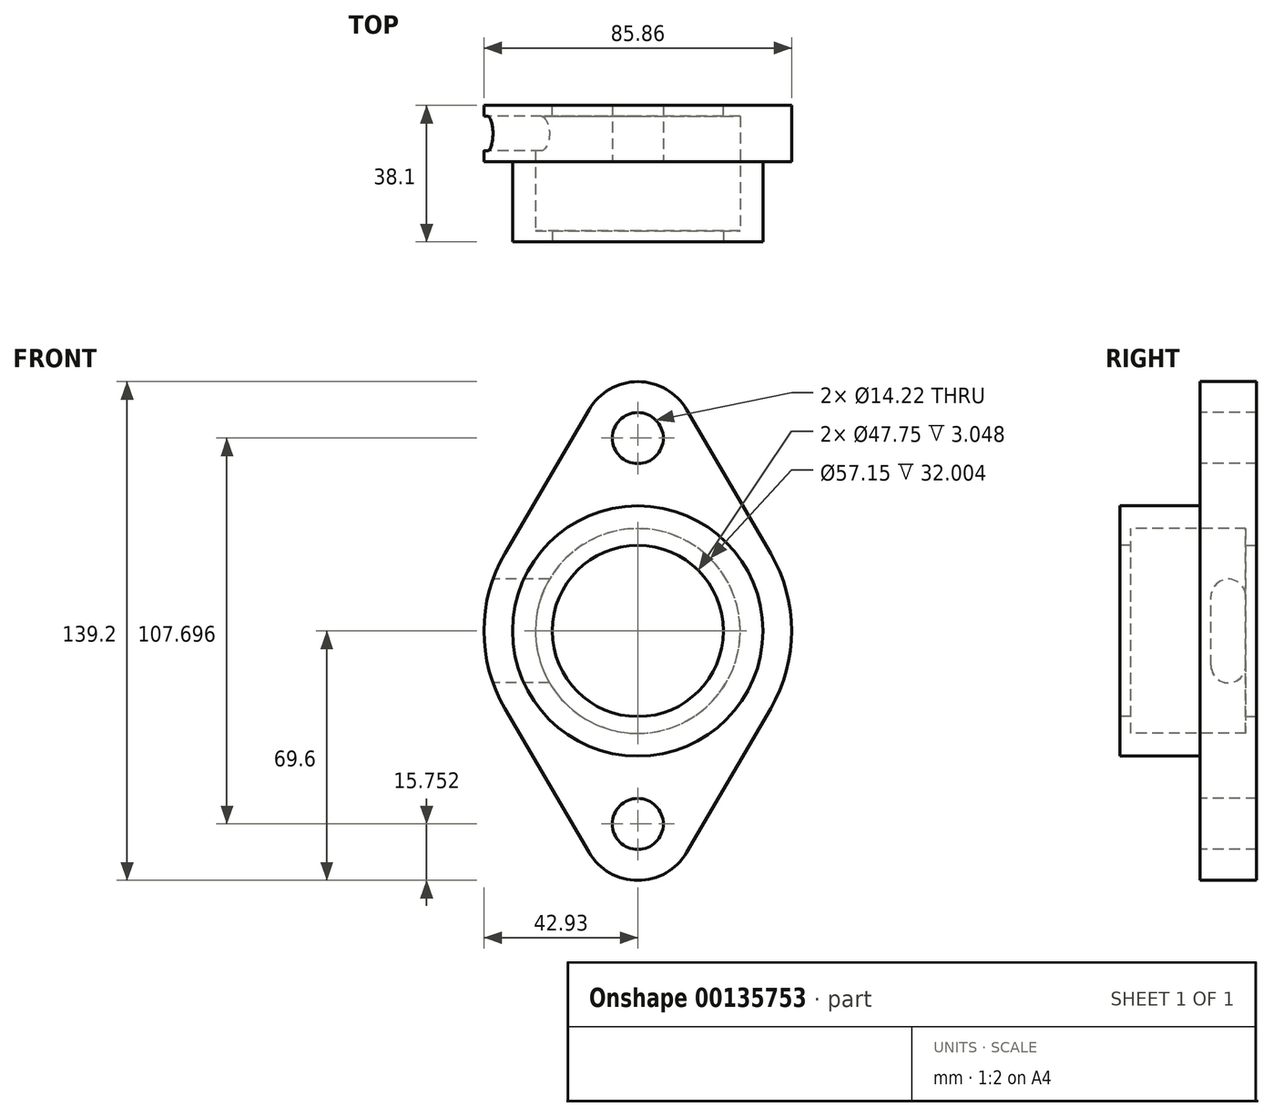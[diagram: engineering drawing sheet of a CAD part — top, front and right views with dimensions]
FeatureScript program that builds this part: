
annotation { "Feature Type Name" : "Feature", "Feature Type Description" : "" }
export const myFeature = defineFeature(function(context is Context, id is Id, definition is map)
    precondition{}
    {
        {
            var Q0;
            Q0=qCreatedBy(makeId("Front.planeOp"),FACE);
            var sketch = newSketch(context, id + "F0", { "sketchPlane" : qUnion([Q0])});
            skArc(sketch, "E0", {"start": v(-37.06, 21.67) * mm, "mid": v(-42.93, 0) * mm, "end": v(-37.06, -21.67) * mm});
            skLineSegment(sketch, "E1", {"start": v(-37.06, 21.67) * mm, "end": v(-13.6, 61.8) * mm});
            skLineSegment(sketch, "E2", {"start": v(37.06, 21.67) * mm, "end": v(13.6, 61.8) * mm});
            skLineSegment(sketch, "E3", {"start": v(-37.06, -21.67) * mm, "end": v(-13.6, -61.8) * mm});
            skLineSegment(sketch, "E4", {"start": v(37.06, -21.67) * mm, "end": v(13.6, -61.8) * mm});
            skArc(sketch, "E5", {"start": v(-13.6, -61.8) * mm, "mid": v(0, -69.6) * mm, "end": v(13.6, -61.8) * mm});
            skCircle(sketch, "E6", {"center": v(0, 53.85) * mm, "radius": 7.11 * mm});
            skArc(sketch, "E7", {"start": v(13.6, 61.8) * mm, "mid": v(0, 69.6) * mm, "end": v(-13.6, 61.8) * mm});
            skCircle(sketch, "E8", {"center": v(0, -53.85) * mm, "radius": 7.11 * mm});
            skArc(sketch, "E9.trimOffspring", {"start": v(37.06, -21.67) * mm, "mid": v(42.93, 0) * mm, "end": v(37.06, 21.67) * mm});
            skLineSegment(sketch, "E10", {"start": v(1.63, 0) * mm, "end": v(40.06, 0) * mm, "construction": true});
            skSolve(sketch);
        }
        {
            var Q0;
            Q0 = qSketchRegion(id + "F0", true);
            extrude(context, id + "F1", {"entities" : qUnion([Q0]), "oppositeDirection" : true, "depth" : 15.75 * mm});
        }
        {
            var Q0;
            Q0=makeQuery(id+"F1.opExtrude","CAP_FACE",FACE,{"disambiguationData":[OSD([sQuery(id+"F0.wireOp",EDGE,"E0"),sQuery(id+"F0.wireOp",EDGE,"E1"),sQuery(id+"F0.wireOp",EDGE,"E2"),sQuery(id+"F0.wireOp",EDGE,"E3"),sQuery(id+"F0.wireOp",EDGE,"E4"),sQuery(id+"F0.wireOp",EDGE,"E5"),sQuery(id+"F0.wireOp",EDGE,"E6"),sQuery(id+"F0.wireOp",EDGE,"E7"),sQuery(id+"F0.wireOp",EDGE,"E8"),sQuery(id+"F0.wireOp",EDGE,"E9.trimOffspring")])],"isStart":true});
            var sketch = newSketch(context, id + "F2", { "sketchPlane" : qUnion([Q0])});
            skCircle(sketch, "E11", {"center": v(0, 0) * mm, "radius": 34.93 * mm});
            skSolve(sketch);
        }
        {
            var Q0;
            Q0 = qSketchRegion(id + "F2", true);
            extrude(context, id + "F3", {"entities" : qUnion([Q0]), "operationType" : NewBodyOperationType.ADD, "depth" : 22.35 * mm});
        }
        {
            var Q0;
            Q0=makeQuery(id+"F3.opExtrude","CAP_FACE",FACE,{"disambiguationData":[OSD([sQuery(id+"F2.wireOp",EDGE,"E11")])],"isStart":false});
            var sketch = newSketch(context, id + "F4", { "sketchPlane" : qUnion([Q0])});
            skCircle(sketch, "E12", {"center": v(0, 0) * mm, "radius": 28.58 * mm});
            skSolve(sketch);
        }
        {
            var Q0;
            Q0 = qSketchRegion(id + "F4", true);
            extrude(context, id + "F5", {"entities" : qUnion([Q0]), "operationType" : NewBodyOperationType.REMOVE, "endBound" : BoundingType.THROUGH_ALL, "oppositeDirection" : true, "depth" : 25.4 * mm});
        }
        {
            var Q0;
            Q0=makeQuery(id+"F3.opExtrude","CAP_FACE",FACE,{"disambiguationData":[OSD([sQuery(id+"F2.wireOp",EDGE,"E11")])],"isStart":false});
            var sketch = newSketch(context, id + "F6", { "sketchPlane" : qUnion([Q0])});
            skCircle(sketch, "E13", {"center": v(0, 0) * mm, "radius": 34.93 * mm});
            skSolve(sketch);
        }
        {
            var Q0;
            Q0 = qSketchRegion(id + "F6", true);
            extrude(context, id + "F7", {"entities" : qUnion([Q0]), "operationType" : NewBodyOperationType.ADD, "oppositeDirection" : true, "depth" : 3.05 * mm});
        }
        {
            var Q0;
            Q0=makeQuery(id+"F7.boolean.opBoolean","MERGE",FACE,{"derivedFrom":[makeQuery(id+"F3.opExtrude","CAP_FACE",FACE,{"disambiguationData":[OSD([sQuery(id+"F2.wireOp",EDGE,"E11")])],"isStart":false}),makeQuery(id+"F7.opExtrude","CAP_FACE",FACE,{"disambiguationData":[OSD([sQuery(id+"F6.wireOp",EDGE,"E13")])],"isStart":true})]});
            var sketch = newSketch(context, id + "F8", { "sketchPlane" : qUnion([Q0])});
            skCircle(sketch, "E14", {"center": v(0, 0) * mm, "radius": 23.88 * mm});
            skSolve(sketch);
        }
        {
            var Q0;
            Q0 = qSketchRegion(id + "F8", true);
            extrude(context, id + "F9", {"entities" : qUnion([Q0]), "operationType" : NewBodyOperationType.REMOVE, "endBound" : BoundingType.THROUGH_ALL, "oppositeDirection" : true, "depth" : 25.4 * mm});
        }
        {
            var Q0;
            Q0=makeQuery(id+"F1.opExtrude","CAP_FACE",FACE,{"disambiguationData":[OSD([sQuery(id+"F0.wireOp",EDGE,"E0"),sQuery(id+"F0.wireOp",EDGE,"E1"),sQuery(id+"F0.wireOp",EDGE,"E2"),sQuery(id+"F0.wireOp",EDGE,"E3"),sQuery(id+"F0.wireOp",EDGE,"E4"),sQuery(id+"F0.wireOp",EDGE,"E5"),sQuery(id+"F0.wireOp",EDGE,"E6"),sQuery(id+"F0.wireOp",EDGE,"E7"),sQuery(id+"F0.wireOp",EDGE,"E8"),sQuery(id+"F0.wireOp",EDGE,"E9.trimOffspring")])],"isStart":false});
            var sketch = newSketch(context, id + "F10", { "sketchPlane" : qUnion([Q0])});
            skCircle(sketch, "E15.0", {"center": v(0, 0) * mm, "radius": 28.58 * mm});
            skSolve(sketch);
        }
        {
            var Q0;
            Q0 = qSketchRegion(id + "F10", true);
            extrude(context, id + "F11", {"entities" : qUnion([Q0]), "operationType" : NewBodyOperationType.ADD, "oppositeDirection" : true, "depth" : 3.05 * mm});
        }
        {
            var Q0;
            Q0=makeQuery(id+"F11.boolean.opBoolean","MERGE",FACE,{"derivedFrom":[makeQuery(id+"F1.opExtrude","CAP_FACE",FACE,{"disambiguationData":[OSD([sQuery(id+"F0.wireOp",EDGE,"E0"),sQuery(id+"F0.wireOp",EDGE,"E1"),sQuery(id+"F0.wireOp",EDGE,"E2"),sQuery(id+"F0.wireOp",EDGE,"E3"),sQuery(id+"F0.wireOp",EDGE,"E4"),sQuery(id+"F0.wireOp",EDGE,"E5"),sQuery(id+"F0.wireOp",EDGE,"E6"),sQuery(id+"F0.wireOp",EDGE,"E7"),sQuery(id+"F0.wireOp",EDGE,"E8"),sQuery(id+"F0.wireOp",EDGE,"E9.trimOffspring")])],"isStart":false}),makeQuery(id+"F11.opExtrude","CAP_FACE",FACE,{"disambiguationData":[OSD([sQuery(id+"F10.wireOp",EDGE,"E15.0")])],"isStart":true})]});
            var sketch = newSketch(context, id + "F12", { "sketchPlane" : qUnion([Q0])});
            skCircle(sketch, "E16", {"center": v(0, 0) * mm, "radius": 23.88 * mm});
            skSolve(sketch);
        }
        {
            var Q0;
            Q0 = qSketchRegion(id + "F12", true);
            extrude(context, id + "F13", {"entities" : qUnion([Q0]), "operationType" : NewBodyOperationType.REMOVE, "endBound" : BoundingType.THROUGH_ALL, "oppositeDirection" : true, "depth" : 25.4 * mm});
        }
        {
            var Q0;
            Q0=qCreatedBy(makeId("Right.planeOp"),FACE);
            cPlane(context, id + "F14", {"entities" : qUnion([Q0]), "cplaneType" : CPlaneType.OFFSET, "offset" : 42.93 * mm, "oppositeDirection" : true, "width" : 152.4 * mm, "height" : 152.4 * mm});
        }
        {
            var Q0;
            Q0=qCreatedBy(id+"F14.planeOp",FACE);
            var sketch = newSketch(context, id + "F15", { "sketchPlane" : qUnion([Q0])});
            skLineSegment(sketch, "E17", {"start": v(12.7, 9.65) * mm, "end": v(12.7, -9.65) * mm});
            skLineSegment(sketch, "E18", {"start": v(3.05, 9.65) * mm, "end": v(3.05, -9.65) * mm});
            skArc(sketch, "E19", {"start": v(12.7, 9.65) * mm, "mid": v(7.87, 14.48) * mm, "end": v(3.05, 9.65) * mm});
            skArc(sketch, "E20", {"start": v(12.7, -9.65) * mm, "mid": v(7.87, -14.48) * mm, "end": v(3.05, -9.65) * mm});
            skSolve(sketch);
        }
        {
            var Q0;
            Q0 = qSketchRegion(id + "F15", true);
            extrude(context, id + "F16", {"entities" : qUnion([Q0]), "operationType" : NewBodyOperationType.REMOVE, "depth" : 42.93 * mm});
        }
    });
